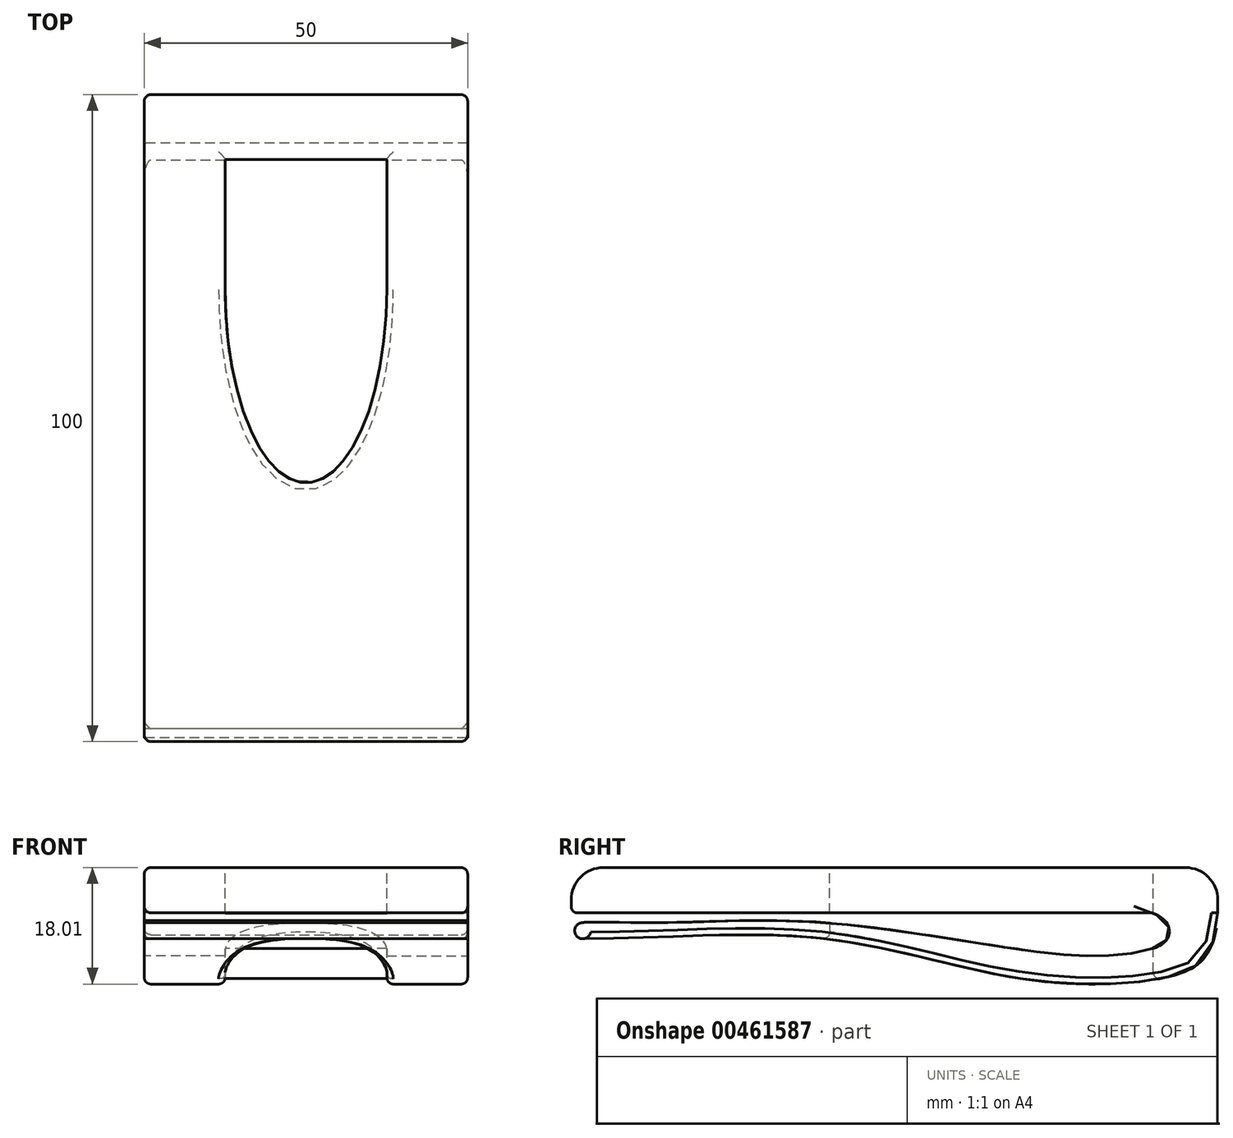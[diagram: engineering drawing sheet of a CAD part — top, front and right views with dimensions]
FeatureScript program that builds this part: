
annotation { "Feature Type Name" : "Feature", "Feature Type Description" : "" }
export const myFeature = defineFeature(function(context is Context, id is Id, definition is map)
    precondition{}
    {
        {
            var Q0;
            Q0=qCreatedBy(makeId("Top.planeOp"),FACE);
            var sketch = newSketch(context, id + "F0", { "sketchPlane" : qUnion([Q0])});
            skLineSegment(sketch, "E0.bottom", {"start": v(25, -50) * mm, "end": v(-25, -50) * mm});
            skLineSegment(sketch, "E0.top", {"start": v(25, 50) * mm, "end": v(-25, 50) * mm});
            skLineSegment(sketch, "E0.left", {"start": v(25, -50) * mm, "end": v(25, 50) * mm});
            skLineSegment(sketch, "E0.right", {"start": v(-25, -50) * mm, "end": v(-25, 50) * mm});
            skPoint(sketch, "E0.middle", {"position": v(0, 0) * mm});
            skSolve(sketch);
        }
        {
            var Q0;
            Q0 = qSketchRegion(id + "F0", true);
            extrude(context, id + "F1", {"entities" : qUnion([Q0]), "depth" : 7 * mm});
        }
        {
            var Q0;
            Q0=qCreatedBy(makeId("Right.planeOp"),FACE);
            var sketch = newSketch(context, id + "F2", { "sketchPlane" : qUnion([Q0])});
            skLineSegment(sketch, "E1.0", {"start": v(-50, 0) * mm, "end": v(50, 0) * mm});
            skPoint(sketch, "E2.0", {"position": v(50, 0) * mm});
            skFitSpline(sketch, "E3", {"points": [v(50, 0) * mm, v(48.21, -6.57) * mm, v(42.52, -9.86) * mm, v(20.53, -10.3) * mm, v(-10.71, -4) * mm, v(-48.04, -4) * mm], "startDerivative": vector(-1.05, -61.1) * mm, "endDerivative": vector(-131.3, 0) * mm});
            skFitSpline(sketch, "E4", {"points": [v(39.87, 0) * mm, v(42.22, -4) * mm, v(34.43, -6.48) * mm, v(21.63, -5.96) * mm, v(-10.86, -1.5) * mm, v(-35.67, -1.5) * mm, v(-48.04, -1.48) * mm, v(-48.04, -1.53) * mm], "startDerivative": vector(79.18, -27.73) * mm, "endDerivative": vector(3.63, -8.07) * mm});
            skArc(sketch, "E5", {"start": v(-48.04, -1.53) * mm, "mid": v(-49.46, -2.76) * mm, "end": v(-48.04, -4) * mm});
            skSolve(sketch);
        }
        {
            var Q0;
            Q0 = qSketchRegion(id + "F2", true);
            extrude(context, id + "F3", {"entities" : qUnion([Q0]), "operationType" : NewBodyOperationType.ADD, "depth" : 25 * mm, "hasSecondDirection" : true, "secondDirectionOppositeDirection" : true, "secondDirectionDepth" : 25 * mm});
        }
        {
            var Q0;
            Q0=makeQuery(id+"F1.opExtrude","CAP_EDGE",EDGE,{"disambiguationData":[OSD([sQuery(id+"F0.wireOp",EDGE,"E0.bottom")])],"isStart":false});
            var Q1;
            Q1=makeQuery(id+"F1.opExtrude","CAP_EDGE",EDGE,{"disambiguationData":[OSD([sQuery(id+"F0.wireOp",EDGE,"E0.top")])],"isStart":false});
            fillet(context, id + "F4", {"entities" : qUnion([Q0, Q1]), "radius" : 5 * mm, "tangentPropagation" : true, "allowEdgeOverflow" : false});
        }
        {
            var Q0;
            Q0=makeQuery(id+"F1.opExtrude","CAP_EDGE",EDGE,{"disambiguationData":[OSD([sQuery(id+"F0.wireOp",EDGE,"E0.bottom")])],"isStart":true});
            var Q1;
            Q1=makeQuery(id+"F1.opExtrude","CAP_EDGE",EDGE,{"disambiguationData":[OSD([sQuery(id+"F0.wireOp",EDGE,"E0.right")])],"isStart":true});
            var Q2;
            Q2=makeQuery(id+"F1.opExtrude","CAP_EDGE",EDGE,{"disambiguationData":[OSD([sQuery(id+"F0.wireOp",EDGE,"E0.right")])],"isStart":false});
            var Q3;
            Q3=makeQuery(id+"F4.opFillet","BLEND_EDGE",EDGE,{"blendedFrom":[makeQuery(id+"F1.opExtrude","CAP_EDGE",EDGE,{"disambiguationData":[OSD([sQuery(id+"F0.wireOp",EDGE,"E0.bottom")])],"isStart":false}),makeQuery(id+"F3.boolean.opBoolean","MERGE",FACE,{"derivedFrom":[makeQuery(id+"F1.opExtrude","SWEPT_FACE",FACE,{"disambiguationData":[OSD([sQuery(id+"F0.wireOp",EDGE,"E0.right")])]}),makeQuery(id+"F3.opExtrude","CAP_FACE",FACE,{"disambiguationData":[OSD([sQuery(id+"F2.wireOp",EDGE,"E1.0"),sQuery(id+"F2.wireOp",EDGE,"E3"),sQuery(id+"F2.wireOp",EDGE,"E4"),sQuery(id+"F2.wireOp",EDGE,"E5")])],"isStart":true})]})],"blendedInto":[makeQuery(id+"F3.boolean.opBoolean","MERGE",FACE,{"derivedFrom":[makeQuery(id+"F1.opExtrude","SWEPT_FACE",FACE,{"disambiguationData":[OSD([sQuery(id+"F0.wireOp",EDGE,"E0.right")])]}),makeQuery(id+"F3.opExtrude","CAP_FACE",FACE,{"disambiguationData":[OSD([sQuery(id+"F2.wireOp",EDGE,"E1.0"),sQuery(id+"F2.wireOp",EDGE,"E3"),sQuery(id+"F2.wireOp",EDGE,"E4"),sQuery(id+"F2.wireOp",EDGE,"E5")])],"isStart":true})]})]});
            var Q4;
            Q4=makeQuery(id+"F1.opExtrude","CAP_EDGE",EDGE,{"disambiguationData":[OSD([sQuery(id+"F0.wireOp",EDGE,"E0.left")])],"isStart":true});
            var Q5;
            Q5=makeQuery(id+"F1.opExtrude","CAP_EDGE",EDGE,{"disambiguationData":[OSD([sQuery(id+"F0.wireOp",EDGE,"E0.left")])],"isStart":false});
            var Q6;
            Q6=makeQuery(id+"F3.opExtrude","CAP_EDGE",EDGE,{"disambiguationData":[OSD([sQuery(id+"F2.wireOp",EDGE,"E3")])],"isStart":false});
            var Q7;
            Q7=makeQuery(id+"F3.opExtrude","CAP_EDGE",EDGE,{"disambiguationData":[OSD([sQuery(id+"F2.wireOp",EDGE,"E3")])],"isStart":true});
            fillet(context, id + "F5", {"entities" : qUnion([Q0, Q1, Q2, Q3, Q4, Q5, Q6, Q7]), "radius" : 1 * mm, "tangentPropagation" : true, "allowEdgeOverflow" : false});
        }
        {
            var Q0;
            Q0=makeQuery(id+"F1.opExtrude","CAP_FACE",FACE,{"disambiguationData":[OSD([sQuery(id+"F0.wireOp",EDGE,"E0.bottom"),sQuery(id+"F0.wireOp",EDGE,"E0.top"),sQuery(id+"F0.wireOp",EDGE,"E0.left"),sQuery(id+"F0.wireOp",EDGE,"E0.right")])],"isStart":false});
            var sketch = newSketch(context, id + "F6", { "sketchPlane" : qUnion([Q0])});
            skEllipticalArc(sketch, "E6", {});
            skLineSegment(sketch, "E7", {"start": v(-12.5, 20) * mm, "end": v(12.5, 20) * mm, "construction": true});
            skLineSegment(sketch, "E8", {"start": v(12.5, 20) * mm, "end": v(12.5, 40) * mm});
            skLineSegment(sketch, "E9", {"start": v(12.5, 40) * mm, "end": v(-12.5, 40) * mm});
            skLineSegment(sketch, "E10", {"start": v(-12.5, 40) * mm, "end": v(-12.5, 20) * mm});
            const initialGuessF6  = {"E6": [0, 0.02, 0, -1, 0.03, 0.0125, 4.71238898038469, 1.5707963267948966]};
            skSetInitialGuess(sketch, initialGuessF6);
            skSolve(sketch);
        }
        {
            var Q0;
            Q0 = qSketchRegion(id + "F6", true);
            extrude(context, id + "F7", {"entities" : qUnion([Q0]), "operationType" : NewBodyOperationType.REMOVE, "oppositeDirection" : true, "depth" : 25 * mm});
        }
        {
            var Q0;
            Q0=makeQuery(id+"F7.boolean.opBoolean","INTERSECT",EDGE,{"derivedFrom":[makeQuery(id+"F3.opExtrude","SWEPT_FACE",FACE,{"disambiguationData":[OSD([sQuery(id+"F2.wireOp",EDGE,"E3")])]}),makeQuery(id+"F7.opExtrude","SWEPT_FACE",FACE,{"disambiguationData":[OSD([sQuery(id+"F6.wireOp",EDGE,"E9")])]})]});
            var Q1;
            Q1=makeQuery(id+"F7.boolean.opBoolean","INTERSECT",EDGE,{"derivedFrom":[makeQuery(id+"F3.opExtrude","SWEPT_FACE",FACE,{"disambiguationData":[OSD([sQuery(id+"F2.wireOp",EDGE,"E3")])]}),makeQuery(id+"F7.opExtrude","SWEPT_FACE",FACE,{"disambiguationData":[OSD([sQuery(id+"F6.wireOp",EDGE,"E8")])]})]});
            var Q2;
            Q2=makeQuery(id+"F7.boolean.opBoolean","INTERSECT",EDGE,{"derivedFrom":[makeQuery(id+"F3.opExtrude","SWEPT_FACE",FACE,{"disambiguationData":[OSD([sQuery(id+"F2.wireOp",EDGE,"E3")])]}),makeQuery(id+"F7.opExtrude","SWEPT_FACE",FACE,{"disambiguationData":[OSD([sQuery(id+"F6.wireOp",EDGE,"E10")])]})]});
            fillet(context, id + "F8", {"entities" : qUnion([Q0, Q1, Q2]), "radius" : 1 * mm, "tangentPropagation" : true, "allowEdgeOverflow" : false});
        }
    });
